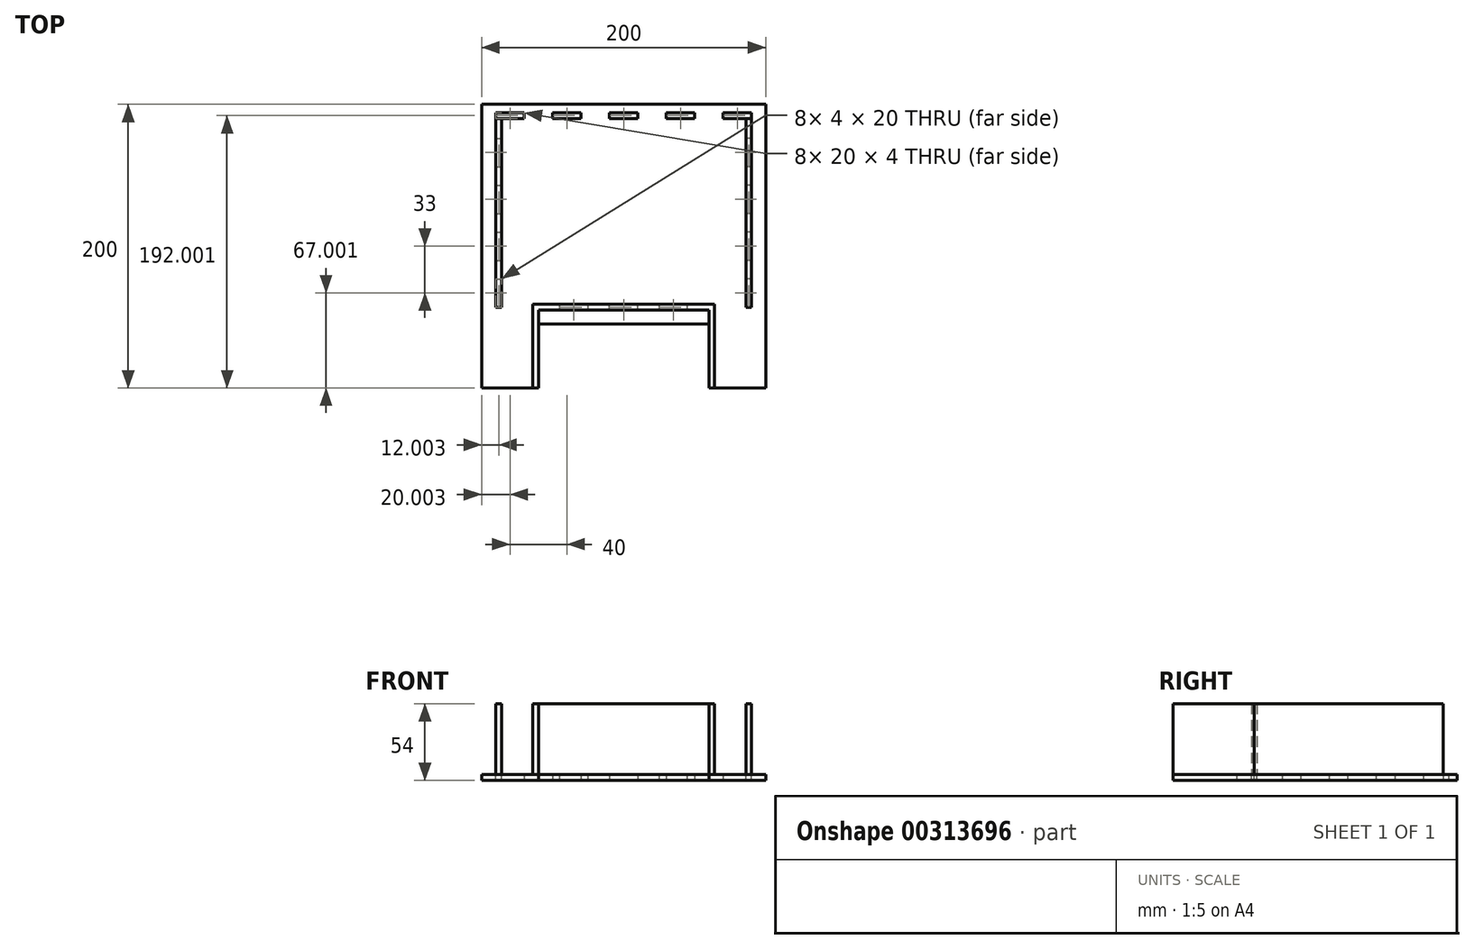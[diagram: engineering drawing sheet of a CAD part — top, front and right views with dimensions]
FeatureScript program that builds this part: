
annotation { "Feature Type Name" : "Feature", "Feature Type Description" : "" }
export const myFeature = defineFeature(function(context is Context, id is Id, definition is map)
    precondition{}
    {
        {
            var Q0;
            Q0=qCreatedBy(makeId("Top.planeOp"),FACE);
            var sketch = newSketch(context, id + "F0", { "sketchPlane" : qUnion([Q0])});
            skLineSegment(sketch, "E0.bottom", {"start": v(-97.63, 105.11) * mm, "end": v(102.37, 105.11) * mm});
            skLineSegment(sketch, "E0.top", {"start": v(-97.63, -94.89) * mm, "end": v(102.37, -94.89) * mm});
            skLineSegment(sketch, "E0.left", {"start": v(-97.63, 105.11) * mm, "end": v(-97.63, -94.89) * mm});
            skLineSegment(sketch, "E0.right", {"start": v(102.37, 105.11) * mm, "end": v(102.37, -94.89) * mm});
            skPoint(sketch, "E0.middle", {"position": v(2.37, 5.11) * mm});
            skLineSegment(sketch, "E1", {"start": v(2.37, -94.89) * mm, "end": v(2.37, 90.11) * mm, "construction": true});
            skLineSegment(sketch, "E2", {"start": v(2.37, 105.11) * mm, "end": v(2.37, 99.11) * mm, "construction": true});
            skLineSegment(sketch, "E3.direction2", {"start": v(12.37, 90.11) * mm, "end": v(13.2, -89.89) * mm, "construction": true});
            skLineSegment(sketch, "E4", {"start": v(102.37, 5.11) * mm, "end": v(92.37, 5.11) * mm, "construction": true});
            skLineSegment(sketch, "E5", {"start": v(92.37, 5.11) * mm, "end": v(102.37, 5.11) * mm, "construction": true});
            skLineSegment(sketch, "E6.top", {"start": v(92.37, -4.89) * mm, "end": v(88.37, -4.89) * mm});
            skLineSegment(sketch, "E6.left", {"start": v(92.37, 5.11) * mm, "end": v(92.37, -4.89) * mm});
            skLineSegment(sketch, "E6.right", {"start": v(88.37, 5.11) * mm, "end": v(88.37, -4.89) * mm});
            skLineSegment(sketch, "E7.MirrorCS", {"start": v(88.37, 5.11) * mm, "end": v(88.37, 15.11) * mm});
            skLineSegment(sketch, "E8.MirrorCS", {"start": v(92.37, 5.11) * mm, "end": v(92.37, 15.11) * mm});
            skLineSegment(sketch, "E9.MirrorCS", {"start": v(92.37, 15.11) * mm, "end": v(88.37, 15.11) * mm});
            skLineSegment(sketch, "E10.trimOffspring", {"start": v(88.37, 5.11) * mm, "end": v(-97.63, 5.11) * mm, "construction": true});
            skLineSegment(sketch, "E11.0.1.0", {"start": v(88.37, 38.11) * mm, "end": v(88.37, 48.11) * mm});
            skLineSegment(sketch, "E11.0.1.1", {"start": v(92.37, 48.11) * mm, "end": v(88.37, 48.11) * mm});
            skLineSegment(sketch, "E11.0.1.2", {"start": v(92.37, 38.11) * mm, "end": v(92.37, 28.11) * mm});
            skLineSegment(sketch, "E11.0.1.3", {"start": v(88.37, 38.11) * mm, "end": v(88.37, 28.11) * mm});
            skLineSegment(sketch, "E11.0.1.4", {"start": v(92.37, 28.11) * mm, "end": v(88.37, 28.11) * mm});
            skLineSegment(sketch, "E11.0.1.5", {"start": v(92.37, 38.11) * mm, "end": v(92.37, 48.11) * mm});
            skLineSegment(sketch, "E11.0.2.0", {"start": v(88.37, 71.11) * mm, "end": v(88.37, 81.11) * mm});
            skLineSegment(sketch, "E11.0.2.1", {"start": v(92.37, 81.11) * mm, "end": v(88.37, 81.11) * mm});
            skLineSegment(sketch, "E11.0.2.2", {"start": v(92.37, 71.11) * mm, "end": v(92.37, 61.11) * mm});
            skLineSegment(sketch, "E11.0.2.3", {"start": v(88.37, 71.11) * mm, "end": v(88.37, 61.11) * mm});
            skLineSegment(sketch, "E11.0.2.4", {"start": v(92.37, 61.11) * mm, "end": v(88.37, 61.11) * mm});
            skLineSegment(sketch, "E11.0.2.5", {"start": v(92.37, 71.11) * mm, "end": v(92.37, 81.11) * mm});
            skLineSegment(sketch, "E11.direction1", {"start": v(88.37, 5.11) * mm, "end": v(112.37, 5.11) * mm, "construction": true});
            skLineSegment(sketch, "E11.direction2", {"start": v(88.37, 5.11) * mm, "end": v(88.37, 38.11) * mm, "construction": true});
            skLineSegment(sketch, "E12.MirrorCS", {"start": v(92.37, -27.89) * mm, "end": v(92.37, -37.89) * mm});
            skLineSegment(sketch, "E13.MirrorCS", {"start": v(92.37, -17.89) * mm, "end": v(88.37, -17.89) * mm});
            skLineSegment(sketch, "E14.MirrorCS", {"start": v(88.37, -27.89) * mm, "end": v(88.37, -17.89) * mm});
            skLineSegment(sketch, "E15.MirrorCS", {"start": v(88.37, -27.89) * mm, "end": v(88.37, -37.89) * mm});
            skLineSegment(sketch, "E16.MirrorCS", {"start": v(92.37, -27.89) * mm, "end": v(92.37, -17.89) * mm});
            skLineSegment(sketch, "E17.MirrorCS", {"start": v(92.37, -37.89) * mm, "end": v(88.37, -37.89) * mm});
            skLineSegment(sketch, "E18.MirrorCS", {"start": v(-87.63, 15.11) * mm, "end": v(-83.63, 15.11) * mm});
            skLineSegment(sketch, "E19.MirrorCS", {"start": v(-87.63, -27.89) * mm, "end": v(-87.63, -17.89) * mm});
            skLineSegment(sketch, "E20.MirrorCS", {"start": v(-87.63, -17.89) * mm, "end": v(-83.63, -17.89) * mm});
            skLineSegment(sketch, "E21.MirrorCS", {"start": v(-87.63, 28.11) * mm, "end": v(-83.63, 28.11) * mm});
            skLineSegment(sketch, "E22.MirrorCS", {"start": v(-87.63, 81.11) * mm, "end": v(-83.63, 81.11) * mm});
            skLineSegment(sketch, "E23.MirrorCS", {"start": v(-87.63, -4.89) * mm, "end": v(-83.63, -4.89) * mm});
            skLineSegment(sketch, "E24.MirrorCS", {"start": v(-87.63, -37.89) * mm, "end": v(-83.63, -37.89) * mm});
            skLineSegment(sketch, "E25.MirrorCS", {"start": v(-83.63, 71.11) * mm, "end": v(-83.63, 61.11) * mm});
            skLineSegment(sketch, "E26.MirrorCS", {"start": v(-87.63, 61.11) * mm, "end": v(-83.63, 61.11) * mm});
            skLineSegment(sketch, "E27.MirrorCS", {"start": v(-87.63, 48.11) * mm, "end": v(-83.63, 48.11) * mm});
            skLineSegment(sketch, "E28.MirrorCS", {"start": v(-87.63, 71.11) * mm, "end": v(-87.63, 61.11) * mm});
            skLineSegment(sketch, "E29.MirrorCS", {"start": v(-83.63, -27.89) * mm, "end": v(-83.63, -17.89) * mm});
            skLineSegment(sketch, "E30.MirrorCS", {"start": v(-83.63, 5.11) * mm, "end": v(-83.63, 15.11) * mm});
            skLineSegment(sketch, "E31.MirrorCS", {"start": v(-83.63, 38.11) * mm, "end": v(-83.63, 28.11) * mm});
            skLineSegment(sketch, "E32.MirrorCS", {"start": v(-87.63, -27.89) * mm, "end": v(-87.63, -37.89) * mm});
            skLineSegment(sketch, "E33.MirrorCS", {"start": v(-87.63, 38.11) * mm, "end": v(-87.63, 48.11) * mm});
            skLineSegment(sketch, "E34.MirrorCS", {"start": v(-83.63, 71.11) * mm, "end": v(-83.63, 81.11) * mm});
            skLineSegment(sketch, "E35.MirrorCS", {"start": v(-83.63, 5.11) * mm, "end": v(-83.63, 38.11) * mm, "construction": true});
            skLineSegment(sketch, "E36.MirrorCS", {"start": v(-87.63, 5.11) * mm, "end": v(-87.63, 15.11) * mm});
            skLineSegment(sketch, "E37.MirrorCS", {"start": v(-83.63, -27.89) * mm, "end": v(-83.63, -37.89) * mm});
            skLineSegment(sketch, "E38.MirrorCS", {"start": v(-87.63, 71.11) * mm, "end": v(-87.63, 81.11) * mm});
            skLineSegment(sketch, "E39.MirrorCS", {"start": v(-83.63, 38.11) * mm, "end": v(-83.63, 48.11) * mm});
            skLineSegment(sketch, "E40.MirrorCS", {"start": v(-83.63, 5.11) * mm, "end": v(-83.63, -4.89) * mm});
            skLineSegment(sketch, "E41.MirrorCS", {"start": v(-87.63, 38.11) * mm, "end": v(-87.63, 28.11) * mm});
            skLineSegment(sketch, "E42.MirrorCS", {"start": v(-87.63, 5.11) * mm, "end": v(-87.63, -4.89) * mm});
            skLineSegment(sketch, "E43.bottom", {"start": v(2.37, 95.11) * mm, "end": v(12.37, 95.11) * mm});
            skLineSegment(sketch, "E43.top", {"start": v(2.37, 99.11) * mm, "end": v(12.37, 99.11) * mm});
            skLineSegment(sketch, "E43.right", {"start": v(12.37, 95.11) * mm, "end": v(12.37, 99.11) * mm});
            skLineSegment(sketch, "E44.MirrorCS", {"start": v(2.37, 99.11) * mm, "end": v(-7.63, 99.11) * mm});
            skLineSegment(sketch, "E45.MirrorCS", {"start": v(-7.63, 95.11) * mm, "end": v(-7.63, 99.11) * mm});
            skLineSegment(sketch, "E46.MirrorCS", {"start": v(2.37, 95.11) * mm, "end": v(-7.63, 95.11) * mm});
            skPoint(sketch, "E47.orphan", {"position": v(2.37, 95.11) * mm});
            skLineSegment(sketch, "E48.1.0.0", {"start": v(42.37, 95.11) * mm, "end": v(32.37, 95.11) * mm});
            skLineSegment(sketch, "E48.1.0.1", {"start": v(32.37, 95.11) * mm, "end": v(32.37, 99.11) * mm});
            skLineSegment(sketch, "E48.1.0.2", {"start": v(52.37, 95.11) * mm, "end": v(52.37, 99.11) * mm});
            skLineSegment(sketch, "E48.1.0.3", {"start": v(42.37, 95.11) * mm, "end": v(52.37, 95.11) * mm});
            skLineSegment(sketch, "E48.1.0.4", {"start": v(42.37, 99.11) * mm, "end": v(32.37, 99.11) * mm});
            skLineSegment(sketch, "E48.1.0.5", {"start": v(42.37, 99.11) * mm, "end": v(52.37, 99.11) * mm});
            skPoint(sketch, "E48.1.0.6", {"position": v(42.37, 95.11) * mm});
            skLineSegment(sketch, "E48.2.0.0", {"start": v(82.37, 95.11) * mm, "end": v(72.37, 95.11) * mm});
            skLineSegment(sketch, "E48.2.0.1", {"start": v(72.37, 95.11) * mm, "end": v(72.37, 99.11) * mm});
            skLineSegment(sketch, "E48.2.0.2", {"start": v(92.37, 95.11) * mm, "end": v(92.37, 99.11) * mm});
            skLineSegment(sketch, "E48.2.0.3", {"start": v(82.37, 95.11) * mm, "end": v(92.37, 95.11) * mm});
            skLineSegment(sketch, "E48.2.0.4", {"start": v(82.37, 99.11) * mm, "end": v(72.37, 99.11) * mm});
            skLineSegment(sketch, "E48.2.0.5", {"start": v(82.37, 99.11) * mm, "end": v(92.37, 99.11) * mm});
            skPoint(sketch, "E48.2.0.6", {"position": v(82.37, 95.11) * mm});
            skLineSegment(sketch, "E48.direction1", {"start": v(-7.63, 95.11) * mm, "end": v(32.37, 95.11) * mm, "construction": true});
            skPoint(sketch, "E49.MirrorP", {"position": v(-37.63, 95.11) * mm});
            skLineSegment(sketch, "E50.MirrorCS", {"start": v(-77.63, 95.11) * mm, "end": v(-87.63, 95.11) * mm});
            skLineSegment(sketch, "E51.MirrorCS", {"start": v(-37.63, 95.11) * mm, "end": v(-47.63, 95.11) * mm});
            skLineSegment(sketch, "E52.MirrorCS", {"start": v(-47.63, 95.11) * mm, "end": v(-47.63, 99.11) * mm});
            skLineSegment(sketch, "E53.MirrorCS", {"start": v(-77.63, 95.11) * mm, "end": v(-67.63, 95.11) * mm});
            skLineSegment(sketch, "E54.MirrorCS", {"start": v(-37.63, 99.11) * mm, "end": v(-47.63, 99.11) * mm});
            skLineSegment(sketch, "E55.MirrorCS", {"start": v(-37.63, 99.11) * mm, "end": v(-27.63, 99.11) * mm});
            skLineSegment(sketch, "E56.MirrorCS", {"start": v(-77.63, 99.11) * mm, "end": v(-87.63, 99.11) * mm});
            skLineSegment(sketch, "E57.MirrorCS", {"start": v(-77.63, 99.11) * mm, "end": v(-67.63, 99.11) * mm});
            skLineSegment(sketch, "E58.MirrorCS", {"start": v(-87.63, 95.11) * mm, "end": v(-87.63, 99.11) * mm});
            skPoint(sketch, "E59.MirrorP", {"position": v(-77.63, 95.11) * mm});
            skLineSegment(sketch, "E60.MirrorCS", {"start": v(-27.63, 95.11) * mm, "end": v(-27.63, 99.11) * mm});
            skLineSegment(sketch, "E61.MirrorCS", {"start": v(-67.63, 95.11) * mm, "end": v(-67.63, 99.11) * mm});
            skLineSegment(sketch, "E62.MirrorCS", {"start": v(-37.63, 95.11) * mm, "end": v(-27.63, 95.11) * mm});
            skLineSegment(sketch, "E63.MirrorCS", {"start": v(-83.63, 5.11) * mm, "end": v(102.37, 5.11) * mm, "construction": true});
            skSolve(sketch);
        }
        {
            var Q0;
            Q0=qSketchRegion(id+"F0",true);
            extrude(context, id + "F1", {"entities" : qUnion([Q0]), "endBound" : BoundingType.SYMMETRIC, "depth" : 4 * mm});
        }
        {
            var Q0;
            Q0=makeQuery(id+"F1.opExtrude","CAP_FACE",FACE,{"disambiguationData":[OSD([sQuery(id+"F0.wireOp",EDGE,"E0.bottom"),sQuery(id+"F0.wireOp",EDGE,"E0.top"),sQuery(id+"F0.wireOp",EDGE,"E0.left"),sQuery(id+"F0.wireOp",EDGE,"E0.right"),sQuery(id+"F0.wireOp",EDGE,"E6.top"),sQuery(id+"F0.wireOp",EDGE,"E6.left"),sQuery(id+"F0.wireOp",EDGE,"E6.right"),sQuery(id+"F0.wireOp",EDGE,"E7.MirrorCS"),sQuery(id+"F0.wireOp",EDGE,"E8.MirrorCS"),sQuery(id+"F0.wireOp",EDGE,"E9.MirrorCS"),sQuery(id+"F0.wireOp",EDGE,"E11.0.1.0"),sQuery(id+"F0.wireOp",EDGE,"E11.0.1.1"),sQuery(id+"F0.wireOp",EDGE,"E11.0.1.2"),sQuery(id+"F0.wireOp",EDGE,"E11.0.1.3"),sQuery(id+"F0.wireOp",EDGE,"E11.0.1.4"),sQuery(id+"F0.wireOp",EDGE,"E11.0.1.5"),sQuery(id+"F0.wireOp",EDGE,"E11.0.2.0"),sQuery(id+"F0.wireOp",EDGE,"E11.0.2.1"),sQuery(id+"F0.wireOp",EDGE,"E11.0.2.2"),sQuery(id+"F0.wireOp",EDGE,"E11.0.2.3"),sQuery(id+"F0.wireOp",EDGE,"E11.0.2.4"),sQuery(id+"F0.wireOp",EDGE,"E11.0.2.5"),sQuery(id+"F0.wireOp",EDGE,"E12.MirrorCS"),sQuery(id+"F0.wireOp",EDGE,"E13.MirrorCS"),sQuery(id+"F0.wireOp",EDGE,"a5cf8296-6a1a-48b5-a17e-63ac2f100e7a.MirrorCS"),sQuery(id+"F0.wireOp",EDGE,"6454bcc7-548b-423b-bd61-f2daa2ac8bc2.MirrorCS"),sQuery(id+"F0.wireOp",EDGE,"E14.MirrorCS"),sQuery(id+"F0.wireOp",EDGE,"9c8714bc-c0c6-4e73-bc6f-7604c54330c3.MirrorCS"),sQuery(id+"F0.wireOp",EDGE,"E15.MirrorCS"),sQuery(id+"F0.wireOp",EDGE,"E16.MirrorCS"),sQuery(id+"F0.wireOp",EDGE,"13b4a6b3-9c6c-4970-82ba-403fbf399970.MirrorCS"),sQuery(id+"F0.wireOp",EDGE,"51e258c3-53c8-4c74-be8b-1a210a0881ed.MirrorCS"),sQuery(id+"F0.wireOp",EDGE,"466627d0-206a-413f-a7e9-9d98ee74cc6c.MirrorCS"),sQuery(id+"F0.wireOp",EDGE,"E17.MirrorCS"),sQuery(id+"F0.wireOp",EDGE,"E18.MirrorCS"),sQuery(id+"F0.wireOp",EDGE,"E19.MirrorCS"),sQuery(id+"F0.wireOp",EDGE,"E20.MirrorCS"),sQuery(id+"F0.wireOp",EDGE,"f82beb81-8050-46b6-9a8f-d50cd8b2f4aa.MirrorCS"),sQuery(id+"F0.wireOp",EDGE,"E21.MirrorCS"),sQuery(id+"F0.wireOp",EDGE,"E22.MirrorCS"),sQuery(id+"F0.wireOp",EDGE,"E23.MirrorCS"),sQuery(id+"F0.wireOp",EDGE,"E24.MirrorCS"),sQuery(id+"F0.wireOp",EDGE,"350f11ef-bac5-4566-a7bd-23c74bd45e33.MirrorCS"),sQuery(id+"F0.wireOp",EDGE,"E25.MirrorCS"),sQuery(id+"F0.wireOp",EDGE,"579f2c8e-3274-4fd2-a240-7e44fb226743.MirrorCS"),sQuery(id+"F0.wireOp",EDGE,"E26.MirrorCS"),sQuery(id+"F0.wireOp",EDGE,"24017de7-ebaf-49ac-bcd0-21bb546df799.MirrorCS"),sQuery(id+"F0.wireOp",EDGE,"E27.MirrorCS"),sQuery(id+"F0.wireOp",EDGE,"E28.MirrorCS"),sQuery(id+"F0.wireOp",EDGE,"E29.MirrorCS"),sQuery(id+"F0.wireOp",EDGE,"E30.MirrorCS"),sQuery(id+"F0.wireOp",EDGE,"E31.MirrorCS"),sQuery(id+"F0.wireOp",EDGE,"E32.MirrorCS"),sQuery(id+"F0.wireOp",EDGE,"E33.MirrorCS"),sQuery(id+"F0.wireOp",EDGE,"6270afa9-d4fe-4bc2-898e-67fac00a2f92.MirrorCS"),sQuery(id+"F0.wireOp",EDGE,"E34.MirrorCS"),sQuery(id+"F0.wireOp",EDGE,"E36.MirrorCS"),sQuery(id+"F0.wireOp",EDGE,"E37.MirrorCS"),sQuery(id+"F0.wireOp",EDGE,"E38.MirrorCS"),sQuery(id+"F0.wireOp",EDGE,"E39.MirrorCS"),sQuery(id+"F0.wireOp",EDGE,"E40.MirrorCS"),sQuery(id+"F0.wireOp",EDGE,"E41.MirrorCS"),sQuery(id+"F0.wireOp",EDGE,"E42.MirrorCS"),sQuery(id+"F0.wireOp",EDGE,"c7332622-d526-407a-969b-2bd519e8cb4e.MirrorCS"),sQuery(id+"F0.wireOp",EDGE,"E43.bottom"),sQuery(id+"F0.wireOp",EDGE,"E43.top"),sQuery(id+"F0.wireOp",EDGE,"E43.right"),sQuery(id+"F0.wireOp",EDGE,"E44.MirrorCS"),sQuery(id+"F0.wireOp",EDGE,"E45.MirrorCS"),sQuery(id+"F0.wireOp",EDGE,"E46.MirrorCS"),sQuery(id+"F0.wireOp",EDGE,"E48.1.0.0"),sQuery(id+"F0.wireOp",EDGE,"E48.1.0.1"),sQuery(id+"F0.wireOp",EDGE,"E48.1.0.2"),sQuery(id+"F0.wireOp",EDGE,"E48.1.0.3"),sQuery(id+"F0.wireOp",EDGE,"E48.1.0.4"),sQuery(id+"F0.wireOp",EDGE,"E48.1.0.5"),sQuery(id+"F0.wireOp",EDGE,"E48.2.0.0"),sQuery(id+"F0.wireOp",EDGE,"E48.2.0.1"),sQuery(id+"F0.wireOp",EDGE,"E48.2.0.2"),sQuery(id+"F0.wireOp",EDGE,"E48.2.0.3"),sQuery(id+"F0.wireOp",EDGE,"E48.2.0.4"),sQuery(id+"F0.wireOp",EDGE,"E48.2.0.5"),sQuery(id+"F0.wireOp",EDGE,"E50.MirrorCS"),sQuery(id+"F0.wireOp",EDGE,"E51.MirrorCS"),sQuery(id+"F0.wireOp",EDGE,"E52.MirrorCS"),sQuery(id+"F0.wireOp",EDGE,"E53.MirrorCS"),sQuery(id+"F0.wireOp",EDGE,"E54.MirrorCS"),sQuery(id+"F0.wireOp",EDGE,"E55.MirrorCS"),sQuery(id+"F0.wireOp",EDGE,"E56.MirrorCS"),sQuery(id+"F0.wireOp",EDGE,"E57.MirrorCS"),sQuery(id+"F0.wireOp",EDGE,"E58.MirrorCS"),sQuery(id+"F0.wireOp",EDGE,"E60.MirrorCS"),sQuery(id+"F0.wireOp",EDGE,"E61.MirrorCS"),sQuery(id+"F0.wireOp",EDGE,"E62.MirrorCS")])],"isStart":false});
            var sketch = newSketch(context, id + "F2", { "sketchPlane" : qUnion([Q0])});
            skPoint(sketch, "E64", {"position": v(2.37, -94.89) * mm});
            skLineSegment(sketch, "E65", {"start": v(2.37, -94.89) * mm, "end": v(2.37, -49.89) * mm, "construction": true});
            skLineSegment(sketch, "E66", {"start": v(2.37, -49.89) * mm, "end": v(62.37, -49.89) * mm});
            skLineSegment(sketch, "E67", {"start": v(62.37, -49.89) * mm, "end": v(62.37, -94.89) * mm});
            skLineSegment(sketch, "E68", {"start": v(62.37, -94.89) * mm, "end": v(2.37, -94.89) * mm});
            skLineSegment(sketch, "E69.MirrorCS", {"start": v(2.37, -49.89) * mm, "end": v(-57.63, -49.89) * mm});
            skLineSegment(sketch, "E70.MirrorCS", {"start": v(-57.63, -49.89) * mm, "end": v(-57.63, -94.89) * mm});
            skLineSegment(sketch, "E71.MirrorCS", {"start": v(-57.63, -94.89) * mm, "end": v(2.37, -94.89) * mm});
            skSolve(sketch);
        }
        {
            var Q0;
            Q0=qSketchRegion(id+"F2",true);
            var Q1;
            Q1=makeQuery(id+"F1.opExtrude","SWEPT_BODY",BODY,{"disambiguationData":[OSD([sQuery(id+"F0.wireOp",EDGE,"E0.bottom"),sQuery(id+"F0.wireOp",EDGE,"E0.top"),sQuery(id+"F0.wireOp",EDGE,"E0.left"),sQuery(id+"F0.wireOp",EDGE,"E0.right"),sQuery(id+"F0.wireOp",EDGE,"E6.top"),sQuery(id+"F0.wireOp",EDGE,"E6.left"),sQuery(id+"F0.wireOp",EDGE,"E6.right"),sQuery(id+"F0.wireOp",EDGE,"E7.MirrorCS"),sQuery(id+"F0.wireOp",EDGE,"E8.MirrorCS"),sQuery(id+"F0.wireOp",EDGE,"E9.MirrorCS"),sQuery(id+"F0.wireOp",EDGE,"E11.0.1.0"),sQuery(id+"F0.wireOp",EDGE,"E11.0.1.1"),sQuery(id+"F0.wireOp",EDGE,"E11.0.1.2"),sQuery(id+"F0.wireOp",EDGE,"E11.0.1.3"),sQuery(id+"F0.wireOp",EDGE,"E11.0.1.4"),sQuery(id+"F0.wireOp",EDGE,"E11.0.1.5"),sQuery(id+"F0.wireOp",EDGE,"E11.0.2.0"),sQuery(id+"F0.wireOp",EDGE,"E11.0.2.1"),sQuery(id+"F0.wireOp",EDGE,"E11.0.2.2"),sQuery(id+"F0.wireOp",EDGE,"E11.0.2.3"),sQuery(id+"F0.wireOp",EDGE,"E11.0.2.4"),sQuery(id+"F0.wireOp",EDGE,"E11.0.2.5"),sQuery(id+"F0.wireOp",EDGE,"E12.MirrorCS"),sQuery(id+"F0.wireOp",EDGE,"E13.MirrorCS"),sQuery(id+"F0.wireOp",EDGE,"a5cf8296-6a1a-48b5-a17e-63ac2f100e7a.MirrorCS"),sQuery(id+"F0.wireOp",EDGE,"6454bcc7-548b-423b-bd61-f2daa2ac8bc2.MirrorCS"),sQuery(id+"F0.wireOp",EDGE,"E14.MirrorCS"),sQuery(id+"F0.wireOp",EDGE,"9c8714bc-c0c6-4e73-bc6f-7604c54330c3.MirrorCS"),sQuery(id+"F0.wireOp",EDGE,"E15.MirrorCS"),sQuery(id+"F0.wireOp",EDGE,"E16.MirrorCS"),sQuery(id+"F0.wireOp",EDGE,"13b4a6b3-9c6c-4970-82ba-403fbf399970.MirrorCS"),sQuery(id+"F0.wireOp",EDGE,"51e258c3-53c8-4c74-be8b-1a210a0881ed.MirrorCS"),sQuery(id+"F0.wireOp",EDGE,"466627d0-206a-413f-a7e9-9d98ee74cc6c.MirrorCS"),sQuery(id+"F0.wireOp",EDGE,"E17.MirrorCS"),sQuery(id+"F0.wireOp",EDGE,"E18.MirrorCS"),sQuery(id+"F0.wireOp",EDGE,"E19.MirrorCS"),sQuery(id+"F0.wireOp",EDGE,"E20.MirrorCS"),sQuery(id+"F0.wireOp",EDGE,"f82beb81-8050-46b6-9a8f-d50cd8b2f4aa.MirrorCS"),sQuery(id+"F0.wireOp",EDGE,"E21.MirrorCS"),sQuery(id+"F0.wireOp",EDGE,"E22.MirrorCS"),sQuery(id+"F0.wireOp",EDGE,"E23.MirrorCS"),sQuery(id+"F0.wireOp",EDGE,"E24.MirrorCS"),sQuery(id+"F0.wireOp",EDGE,"350f11ef-bac5-4566-a7bd-23c74bd45e33.MirrorCS"),sQuery(id+"F0.wireOp",EDGE,"E25.MirrorCS"),sQuery(id+"F0.wireOp",EDGE,"579f2c8e-3274-4fd2-a240-7e44fb226743.MirrorCS"),sQuery(id+"F0.wireOp",EDGE,"E26.MirrorCS"),sQuery(id+"F0.wireOp",EDGE,"24017de7-ebaf-49ac-bcd0-21bb546df799.MirrorCS"),sQuery(id+"F0.wireOp",EDGE,"E27.MirrorCS"),sQuery(id+"F0.wireOp",EDGE,"E28.MirrorCS"),sQuery(id+"F0.wireOp",EDGE,"E29.MirrorCS"),sQuery(id+"F0.wireOp",EDGE,"E30.MirrorCS"),sQuery(id+"F0.wireOp",EDGE,"E31.MirrorCS"),sQuery(id+"F0.wireOp",EDGE,"E32.MirrorCS"),sQuery(id+"F0.wireOp",EDGE,"E33.MirrorCS"),sQuery(id+"F0.wireOp",EDGE,"6270afa9-d4fe-4bc2-898e-67fac00a2f92.MirrorCS"),sQuery(id+"F0.wireOp",EDGE,"E34.MirrorCS"),sQuery(id+"F0.wireOp",EDGE,"E36.MirrorCS"),sQuery(id+"F0.wireOp",EDGE,"E37.MirrorCS"),sQuery(id+"F0.wireOp",EDGE,"E38.MirrorCS"),sQuery(id+"F0.wireOp",EDGE,"E39.MirrorCS"),sQuery(id+"F0.wireOp",EDGE,"E40.MirrorCS"),sQuery(id+"F0.wireOp",EDGE,"E41.MirrorCS"),sQuery(id+"F0.wireOp",EDGE,"E42.MirrorCS"),sQuery(id+"F0.wireOp",EDGE,"c7332622-d526-407a-969b-2bd519e8cb4e.MirrorCS"),sQuery(id+"F0.wireOp",EDGE,"E43.bottom"),sQuery(id+"F0.wireOp",EDGE,"E43.top"),sQuery(id+"F0.wireOp",EDGE,"E43.right"),sQuery(id+"F0.wireOp",EDGE,"E44.MirrorCS"),sQuery(id+"F0.wireOp",EDGE,"E45.MirrorCS"),sQuery(id+"F0.wireOp",EDGE,"E46.MirrorCS"),sQuery(id+"F0.wireOp",EDGE,"E48.1.0.0"),sQuery(id+"F0.wireOp",EDGE,"E48.1.0.1"),sQuery(id+"F0.wireOp",EDGE,"E48.1.0.2"),sQuery(id+"F0.wireOp",EDGE,"E48.1.0.3"),sQuery(id+"F0.wireOp",EDGE,"E48.1.0.4"),sQuery(id+"F0.wireOp",EDGE,"E48.1.0.5"),sQuery(id+"F0.wireOp",EDGE,"E48.2.0.0"),sQuery(id+"F0.wireOp",EDGE,"E48.2.0.1"),sQuery(id+"F0.wireOp",EDGE,"E48.2.0.2"),sQuery(id+"F0.wireOp",EDGE,"E48.2.0.3"),sQuery(id+"F0.wireOp",EDGE,"E48.2.0.4"),sQuery(id+"F0.wireOp",EDGE,"E48.2.0.5"),sQuery(id+"F0.wireOp",EDGE,"E50.MirrorCS"),sQuery(id+"F0.wireOp",EDGE,"E51.MirrorCS"),sQuery(id+"F0.wireOp",EDGE,"E52.MirrorCS"),sQuery(id+"F0.wireOp",EDGE,"E53.MirrorCS"),sQuery(id+"F0.wireOp",EDGE,"E54.MirrorCS"),sQuery(id+"F0.wireOp",EDGE,"E55.MirrorCS"),sQuery(id+"F0.wireOp",EDGE,"E56.MirrorCS"),sQuery(id+"F0.wireOp",EDGE,"E57.MirrorCS"),sQuery(id+"F0.wireOp",EDGE,"E58.MirrorCS"),sQuery(id+"F0.wireOp",EDGE,"E60.MirrorCS"),sQuery(id+"F0.wireOp",EDGE,"E61.MirrorCS"),sQuery(id+"F0.wireOp",EDGE,"E62.MirrorCS")])]});
            extrude(context, id + "F3", {"entities" : qUnion([Q0]), "operationType" : NewBodyOperationType.REMOVE, "endBound" : BoundingType.UP_TO_BODY, "oppositeDirection" : true, "endBoundEntityBody" : qUnion([Q1]), "depth" : 25 * mm});
        }
        {
            var Q0;
            Q0=makeQuery(id+"F1.opExtrude","CAP_FACE",FACE,{"disambiguationData":[OSD([sQuery(id+"F0.wireOp",EDGE,"E0.bottom"),sQuery(id+"F0.wireOp",EDGE,"E0.top"),sQuery(id+"F0.wireOp",EDGE,"E0.left"),sQuery(id+"F0.wireOp",EDGE,"E0.right"),sQuery(id+"F0.wireOp",EDGE,"E6.top"),sQuery(id+"F0.wireOp",EDGE,"E6.left"),sQuery(id+"F0.wireOp",EDGE,"E6.right"),sQuery(id+"F0.wireOp",EDGE,"E7.MirrorCS"),sQuery(id+"F0.wireOp",EDGE,"E8.MirrorCS"),sQuery(id+"F0.wireOp",EDGE,"E9.MirrorCS"),sQuery(id+"F0.wireOp",EDGE,"E11.0.1.0"),sQuery(id+"F0.wireOp",EDGE,"E11.0.1.1"),sQuery(id+"F0.wireOp",EDGE,"E11.0.1.2"),sQuery(id+"F0.wireOp",EDGE,"E11.0.1.3"),sQuery(id+"F0.wireOp",EDGE,"E11.0.1.4"),sQuery(id+"F0.wireOp",EDGE,"E11.0.1.5"),sQuery(id+"F0.wireOp",EDGE,"E11.0.2.0"),sQuery(id+"F0.wireOp",EDGE,"E11.0.2.1"),sQuery(id+"F0.wireOp",EDGE,"E11.0.2.2"),sQuery(id+"F0.wireOp",EDGE,"E11.0.2.3"),sQuery(id+"F0.wireOp",EDGE,"E11.0.2.4"),sQuery(id+"F0.wireOp",EDGE,"E11.0.2.5"),sQuery(id+"F0.wireOp",EDGE,"E12.MirrorCS"),sQuery(id+"F0.wireOp",EDGE,"E13.MirrorCS"),sQuery(id+"F0.wireOp",EDGE,"E14.MirrorCS"),sQuery(id+"F0.wireOp",EDGE,"E15.MirrorCS"),sQuery(id+"F0.wireOp",EDGE,"E16.MirrorCS"),sQuery(id+"F0.wireOp",EDGE,"E17.MirrorCS"),sQuery(id+"F0.wireOp",EDGE,"E18.MirrorCS"),sQuery(id+"F0.wireOp",EDGE,"E19.MirrorCS"),sQuery(id+"F0.wireOp",EDGE,"E20.MirrorCS"),sQuery(id+"F0.wireOp",EDGE,"E21.MirrorCS"),sQuery(id+"F0.wireOp",EDGE,"E22.MirrorCS"),sQuery(id+"F0.wireOp",EDGE,"E23.MirrorCS"),sQuery(id+"F0.wireOp",EDGE,"E24.MirrorCS"),sQuery(id+"F0.wireOp",EDGE,"E25.MirrorCS"),sQuery(id+"F0.wireOp",EDGE,"E26.MirrorCS"),sQuery(id+"F0.wireOp",EDGE,"E27.MirrorCS"),sQuery(id+"F0.wireOp",EDGE,"E28.MirrorCS"),sQuery(id+"F0.wireOp",EDGE,"E29.MirrorCS"),sQuery(id+"F0.wireOp",EDGE,"E30.MirrorCS"),sQuery(id+"F0.wireOp",EDGE,"E31.MirrorCS"),sQuery(id+"F0.wireOp",EDGE,"E32.MirrorCS"),sQuery(id+"F0.wireOp",EDGE,"E33.MirrorCS"),sQuery(id+"F0.wireOp",EDGE,"E34.MirrorCS"),sQuery(id+"F0.wireOp",EDGE,"E36.MirrorCS"),sQuery(id+"F0.wireOp",EDGE,"E37.MirrorCS"),sQuery(id+"F0.wireOp",EDGE,"E38.MirrorCS"),sQuery(id+"F0.wireOp",EDGE,"E39.MirrorCS"),sQuery(id+"F0.wireOp",EDGE,"E40.MirrorCS"),sQuery(id+"F0.wireOp",EDGE,"E41.MirrorCS"),sQuery(id+"F0.wireOp",EDGE,"E42.MirrorCS"),sQuery(id+"F0.wireOp",EDGE,"E43.bottom"),sQuery(id+"F0.wireOp",EDGE,"E43.top"),sQuery(id+"F0.wireOp",EDGE,"E43.right"),sQuery(id+"F0.wireOp",EDGE,"E44.MirrorCS"),sQuery(id+"F0.wireOp",EDGE,"E45.MirrorCS"),sQuery(id+"F0.wireOp",EDGE,"E46.MirrorCS"),sQuery(id+"F0.wireOp",EDGE,"E48.1.0.0"),sQuery(id+"F0.wireOp",EDGE,"E48.1.0.1"),sQuery(id+"F0.wireOp",EDGE,"E48.1.0.2"),sQuery(id+"F0.wireOp",EDGE,"E48.1.0.3"),sQuery(id+"F0.wireOp",EDGE,"E48.1.0.4"),sQuery(id+"F0.wireOp",EDGE,"E48.1.0.5"),sQuery(id+"F0.wireOp",EDGE,"E48.2.0.0"),sQuery(id+"F0.wireOp",EDGE,"E48.2.0.1"),sQuery(id+"F0.wireOp",EDGE,"E48.2.0.2"),sQuery(id+"F0.wireOp",EDGE,"E48.2.0.3"),sQuery(id+"F0.wireOp",EDGE,"E48.2.0.4"),sQuery(id+"F0.wireOp",EDGE,"E48.2.0.5"),sQuery(id+"F0.wireOp",EDGE,"E50.MirrorCS"),sQuery(id+"F0.wireOp",EDGE,"E51.MirrorCS"),sQuery(id+"F0.wireOp",EDGE,"E52.MirrorCS"),sQuery(id+"F0.wireOp",EDGE,"E53.MirrorCS"),sQuery(id+"F0.wireOp",EDGE,"E54.MirrorCS"),sQuery(id+"F0.wireOp",EDGE,"E55.MirrorCS"),sQuery(id+"F0.wireOp",EDGE,"E56.MirrorCS"),sQuery(id+"F0.wireOp",EDGE,"E57.MirrorCS"),sQuery(id+"F0.wireOp",EDGE,"E58.MirrorCS"),sQuery(id+"F0.wireOp",EDGE,"E60.MirrorCS"),sQuery(id+"F0.wireOp",EDGE,"E61.MirrorCS"),sQuery(id+"F0.wireOp",EDGE,"E62.MirrorCS")])],"isStart":false});
            var sketch = newSketch(context, id + "F4", { "sketchPlane" : qUnion([Q0])});
            skLineSegment(sketch, "E72", {"start": v(2.37, 95.11) * mm, "end": v(2.37, -49.89) * mm, "construction": true});
            skPoint(sketch, "E73", {"position": v(2.37, -39.89) * mm});
            skLineSegment(sketch, "E74.bottom", {"start": v(2.37, -39.89) * mm, "end": v(-7.63, -39.89) * mm});
            skLineSegment(sketch, "E74.top", {"start": v(2.37, -35.89) * mm, "end": v(-7.63, -35.89) * mm});
            skLineSegment(sketch, "E74.left", {"start": v(2.37, -39.89) * mm, "end": v(2.37, -35.89) * mm});
            skLineSegment(sketch, "E74.right", {"start": v(-7.63, -39.89) * mm, "end": v(-7.63, -35.89) * mm});
            skLineSegment(sketch, "E75.MirrorCS", {"start": v(2.37, -35.89) * mm, "end": v(12.37, -35.89) * mm});
            skLineSegment(sketch, "E76.MirrorCS", {"start": v(2.37, -39.89) * mm, "end": v(12.37, -39.89) * mm});
            skLineSegment(sketch, "E77.MirrorCS", {"start": v(12.37, -39.89) * mm, "end": v(12.37, -35.89) * mm});
            skLineSegment(sketch, "E78.1.0.0", {"start": v(37.37, -35.89) * mm, "end": v(47.37, -35.89) * mm});
            skLineSegment(sketch, "E78.1.0.1", {"start": v(47.37, -39.89) * mm, "end": v(47.37, -35.89) * mm});
            skLineSegment(sketch, "E78.1.0.2", {"start": v(37.37, -39.89) * mm, "end": v(47.37, -39.89) * mm});
            skLineSegment(sketch, "E78.1.0.3", {"start": v(37.37, -39.89) * mm, "end": v(27.37, -39.89) * mm});
            skLineSegment(sketch, "E78.1.0.4", {"start": v(27.37, -39.89) * mm, "end": v(27.37, -35.89) * mm});
            skLineSegment(sketch, "E78.1.0.5", {"start": v(37.37, -35.89) * mm, "end": v(27.37, -35.89) * mm});
            skLineSegment(sketch, "E78.direction1", {"start": v(2.37, -35.89) * mm, "end": v(37.37, -35.89) * mm, "construction": true});
            skLineSegment(sketch, "E79.MirrorCS", {"start": v(-32.63, -39.89) * mm, "end": v(-22.63, -39.89) * mm});
            skLineSegment(sketch, "E80.MirrorCS", {"start": v(-32.63, -39.89) * mm, "end": v(-42.63, -39.89) * mm});
            skLineSegment(sketch, "E81.MirrorCS", {"start": v(-42.63, -39.89) * mm, "end": v(-42.63, -35.89) * mm});
            skLineSegment(sketch, "E82.MirrorCS", {"start": v(-32.63, -35.89) * mm, "end": v(-42.63, -35.89) * mm});
            skLineSegment(sketch, "E83.MirrorCS", {"start": v(-22.63, -39.89) * mm, "end": v(-22.63, -35.89) * mm});
            skLineSegment(sketch, "E84.MirrorCS", {"start": v(2.37, -35.89) * mm, "end": v(-32.63, -35.89) * mm, "construction": true});
            skLineSegment(sketch, "E85", {"start": v(-22.63, -35.89) * mm, "end": v(-32.63, -35.89) * mm});
            skSolve(sketch);
        }
        {
            var Q0;
            Q0=qSketchRegion(id+"F4",true);
            extrude(context, id + "F5", {"entities" : qUnion([Q0]), "operationType" : NewBodyOperationType.REMOVE, "oppositeDirection" : true, "depth" : 25 * mm});
        }
        {
            var Q0;
            Q0=makeQuery(id+"F1.opExtrude","CAP_FACE",FACE,{"disambiguationData":[OSD([sQuery(id+"F0.wireOp",EDGE,"E0.bottom"),sQuery(id+"F0.wireOp",EDGE,"E0.top"),sQuery(id+"F0.wireOp",EDGE,"E0.left"),sQuery(id+"F0.wireOp",EDGE,"E0.right"),sQuery(id+"F0.wireOp",EDGE,"E6.top"),sQuery(id+"F0.wireOp",EDGE,"E6.left"),sQuery(id+"F0.wireOp",EDGE,"E6.right"),sQuery(id+"F0.wireOp",EDGE,"E7.MirrorCS"),sQuery(id+"F0.wireOp",EDGE,"E8.MirrorCS"),sQuery(id+"F0.wireOp",EDGE,"E9.MirrorCS"),sQuery(id+"F0.wireOp",EDGE,"E11.0.1.0"),sQuery(id+"F0.wireOp",EDGE,"E11.0.1.1"),sQuery(id+"F0.wireOp",EDGE,"E11.0.1.2"),sQuery(id+"F0.wireOp",EDGE,"E11.0.1.3"),sQuery(id+"F0.wireOp",EDGE,"E11.0.1.4"),sQuery(id+"F0.wireOp",EDGE,"E11.0.1.5"),sQuery(id+"F0.wireOp",EDGE,"E11.0.2.0"),sQuery(id+"F0.wireOp",EDGE,"E11.0.2.1"),sQuery(id+"F0.wireOp",EDGE,"E11.0.2.2"),sQuery(id+"F0.wireOp",EDGE,"E11.0.2.3"),sQuery(id+"F0.wireOp",EDGE,"E11.0.2.4"),sQuery(id+"F0.wireOp",EDGE,"E11.0.2.5"),sQuery(id+"F0.wireOp",EDGE,"E12.MirrorCS"),sQuery(id+"F0.wireOp",EDGE,"E13.MirrorCS"),sQuery(id+"F0.wireOp",EDGE,"E14.MirrorCS"),sQuery(id+"F0.wireOp",EDGE,"E15.MirrorCS"),sQuery(id+"F0.wireOp",EDGE,"E16.MirrorCS"),sQuery(id+"F0.wireOp",EDGE,"E17.MirrorCS"),sQuery(id+"F0.wireOp",EDGE,"E18.MirrorCS"),sQuery(id+"F0.wireOp",EDGE,"E19.MirrorCS"),sQuery(id+"F0.wireOp",EDGE,"E20.MirrorCS"),sQuery(id+"F0.wireOp",EDGE,"E21.MirrorCS"),sQuery(id+"F0.wireOp",EDGE,"E22.MirrorCS"),sQuery(id+"F0.wireOp",EDGE,"E23.MirrorCS"),sQuery(id+"F0.wireOp",EDGE,"E24.MirrorCS"),sQuery(id+"F0.wireOp",EDGE,"E25.MirrorCS"),sQuery(id+"F0.wireOp",EDGE,"E26.MirrorCS"),sQuery(id+"F0.wireOp",EDGE,"E27.MirrorCS"),sQuery(id+"F0.wireOp",EDGE,"E28.MirrorCS"),sQuery(id+"F0.wireOp",EDGE,"E29.MirrorCS"),sQuery(id+"F0.wireOp",EDGE,"E30.MirrorCS"),sQuery(id+"F0.wireOp",EDGE,"E31.MirrorCS"),sQuery(id+"F0.wireOp",EDGE,"E32.MirrorCS"),sQuery(id+"F0.wireOp",EDGE,"E33.MirrorCS"),sQuery(id+"F0.wireOp",EDGE,"E34.MirrorCS"),sQuery(id+"F0.wireOp",EDGE,"E36.MirrorCS"),sQuery(id+"F0.wireOp",EDGE,"E37.MirrorCS"),sQuery(id+"F0.wireOp",EDGE,"E38.MirrorCS"),sQuery(id+"F0.wireOp",EDGE,"E39.MirrorCS"),sQuery(id+"F0.wireOp",EDGE,"E40.MirrorCS"),sQuery(id+"F0.wireOp",EDGE,"E41.MirrorCS"),sQuery(id+"F0.wireOp",EDGE,"E42.MirrorCS"),sQuery(id+"F0.wireOp",EDGE,"E43.bottom"),sQuery(id+"F0.wireOp",EDGE,"E43.top"),sQuery(id+"F0.wireOp",EDGE,"E43.right"),sQuery(id+"F0.wireOp",EDGE,"E44.MirrorCS"),sQuery(id+"F0.wireOp",EDGE,"E45.MirrorCS"),sQuery(id+"F0.wireOp",EDGE,"E46.MirrorCS"),sQuery(id+"F0.wireOp",EDGE,"E48.1.0.0"),sQuery(id+"F0.wireOp",EDGE,"E48.1.0.1"),sQuery(id+"F0.wireOp",EDGE,"E48.1.0.2"),sQuery(id+"F0.wireOp",EDGE,"E48.1.0.3"),sQuery(id+"F0.wireOp",EDGE,"E48.1.0.4"),sQuery(id+"F0.wireOp",EDGE,"E48.1.0.5"),sQuery(id+"F0.wireOp",EDGE,"E48.2.0.0"),sQuery(id+"F0.wireOp",EDGE,"E48.2.0.1"),sQuery(id+"F0.wireOp",EDGE,"E48.2.0.2"),sQuery(id+"F0.wireOp",EDGE,"E48.2.0.3"),sQuery(id+"F0.wireOp",EDGE,"E48.2.0.4"),sQuery(id+"F0.wireOp",EDGE,"E48.2.0.5"),sQuery(id+"F0.wireOp",EDGE,"E50.MirrorCS"),sQuery(id+"F0.wireOp",EDGE,"E51.MirrorCS"),sQuery(id+"F0.wireOp",EDGE,"E52.MirrorCS"),sQuery(id+"F0.wireOp",EDGE,"E53.MirrorCS"),sQuery(id+"F0.wireOp",EDGE,"E54.MirrorCS"),sQuery(id+"F0.wireOp",EDGE,"E55.MirrorCS"),sQuery(id+"F0.wireOp",EDGE,"E56.MirrorCS"),sQuery(id+"F0.wireOp",EDGE,"E57.MirrorCS"),sQuery(id+"F0.wireOp",EDGE,"E58.MirrorCS"),sQuery(id+"F0.wireOp",EDGE,"E60.MirrorCS"),sQuery(id+"F0.wireOp",EDGE,"E61.MirrorCS"),sQuery(id+"F0.wireOp",EDGE,"E62.MirrorCS")])],"isStart":false});
            var sketch = newSketch(context, id + "F6", { "sketchPlane" : qUnion([Q0])});
            skLineSegment(sketch, "E86.bottom", {"start": v(-83.63, 81.11) * mm, "end": v(-87.63, 81.11) * mm});
            skLineSegment(sketch, "E86.top", {"start": v(-83.63, 61.11) * mm, "end": v(-87.63, 61.11) * mm});
            skLineSegment(sketch, "E86.left", {"start": v(-83.63, 81.11) * mm, "end": v(-83.63, 61.11) * mm});
            skLineSegment(sketch, "E86.right", {"start": v(-87.63, 81.11) * mm, "end": v(-87.63, 61.11) * mm});
            skLineSegment(sketch, "E87.bottom", {"start": v(-83.63, 48.11) * mm, "end": v(-87.63, 48.11) * mm});
            skLineSegment(sketch, "E87.top", {"start": v(-83.63, 28.11) * mm, "end": v(-87.63, 28.11) * mm});
            skLineSegment(sketch, "E87.left", {"start": v(-83.63, 48.11) * mm, "end": v(-83.63, 28.11) * mm});
            skLineSegment(sketch, "E87.right", {"start": v(-87.63, 48.11) * mm, "end": v(-87.63, 28.11) * mm});
            skLineSegment(sketch, "E88.bottom", {"start": v(-83.63, 15.11) * mm, "end": v(-87.63, 15.11) * mm});
            skLineSegment(sketch, "E88.top", {"start": v(-83.63, -4.89) * mm, "end": v(-87.63, -4.89) * mm});
            skLineSegment(sketch, "E88.left", {"start": v(-83.63, 15.11) * mm, "end": v(-83.63, -4.89) * mm});
            skLineSegment(sketch, "E88.right", {"start": v(-87.63, 15.11) * mm, "end": v(-87.63, -4.89) * mm});
            skLineSegment(sketch, "E89.bottom", {"start": v(-83.63, -17.89) * mm, "end": v(-87.63, -17.89) * mm});
            skLineSegment(sketch, "E89.top", {"start": v(-83.63, -37.89) * mm, "end": v(-87.63, -37.89) * mm});
            skLineSegment(sketch, "E89.left", {"start": v(-83.63, -17.89) * mm, "end": v(-83.63, -37.89) * mm});
            skLineSegment(sketch, "E89.right", {"start": v(-87.63, -17.89) * mm, "end": v(-87.63, -37.89) * mm});
            skLineSegment(sketch, "E90.bottom", {"start": v(-42.63, -39.89) * mm, "end": v(-22.63, -39.89) * mm});
            skLineSegment(sketch, "E90.top", {"start": v(-42.63, -35.89) * mm, "end": v(-22.63, -35.89) * mm});
            skLineSegment(sketch, "E90.left", {"start": v(-42.63, -39.89) * mm, "end": v(-42.63, -35.89) * mm});
            skLineSegment(sketch, "E90.right", {"start": v(-22.63, -39.89) * mm, "end": v(-22.63, -35.89) * mm});
            skLineSegment(sketch, "E91.bottom", {"start": v(-7.63, -39.89) * mm, "end": v(12.37, -39.89) * mm});
            skLineSegment(sketch, "E91.top", {"start": v(-7.63, -35.89) * mm, "end": v(12.37, -35.89) * mm});
            skLineSegment(sketch, "E91.left", {"start": v(-7.63, -39.89) * mm, "end": v(-7.63, -35.89) * mm});
            skLineSegment(sketch, "E91.right", {"start": v(12.37, -39.89) * mm, "end": v(12.37, -35.89) * mm});
            skLineSegment(sketch, "E92.bottom", {"start": v(27.37, -39.89) * mm, "end": v(47.37, -39.89) * mm});
            skLineSegment(sketch, "E92.top", {"start": v(27.37, -35.89) * mm, "end": v(47.37, -35.89) * mm});
            skLineSegment(sketch, "E92.left", {"start": v(27.37, -39.89) * mm, "end": v(27.37, -35.89) * mm});
            skLineSegment(sketch, "E92.right", {"start": v(47.37, -39.89) * mm, "end": v(47.37, -35.89) * mm});
            skLineSegment(sketch, "E93.bottom", {"start": v(92.37, -37.89) * mm, "end": v(88.37, -37.89) * mm});
            skLineSegment(sketch, "E93.top", {"start": v(92.37, -17.89) * mm, "end": v(88.37, -17.89) * mm});
            skLineSegment(sketch, "E93.left", {"start": v(92.37, -37.89) * mm, "end": v(92.37, -17.89) * mm});
            skLineSegment(sketch, "E93.right", {"start": v(88.37, -37.89) * mm, "end": v(88.37, -17.89) * mm});
            skLineSegment(sketch, "E94.bottom", {"start": v(92.37, -4.89) * mm, "end": v(88.37, -4.89) * mm});
            skLineSegment(sketch, "E94.top", {"start": v(92.37, 15.11) * mm, "end": v(88.37, 15.11) * mm});
            skLineSegment(sketch, "E94.left", {"start": v(92.37, -4.89) * mm, "end": v(92.37, 15.11) * mm});
            skLineSegment(sketch, "E94.right", {"start": v(88.37, -4.89) * mm, "end": v(88.37, 15.11) * mm});
            skLineSegment(sketch, "E95.bottom", {"start": v(92.37, 28.11) * mm, "end": v(88.37, 28.11) * mm});
            skLineSegment(sketch, "E95.top", {"start": v(92.37, 48.11) * mm, "end": v(88.37, 48.11) * mm});
            skLineSegment(sketch, "E95.left", {"start": v(92.37, 28.11) * mm, "end": v(92.37, 48.11) * mm});
            skLineSegment(sketch, "E95.right", {"start": v(88.37, 28.11) * mm, "end": v(88.37, 48.11) * mm});
            skLineSegment(sketch, "E96.bottom", {"start": v(92.37, 61.11) * mm, "end": v(88.37, 61.11) * mm});
            skLineSegment(sketch, "E96.top", {"start": v(92.37, 81.11) * mm, "end": v(88.37, 81.11) * mm});
            skLineSegment(sketch, "E96.left", {"start": v(92.37, 61.11) * mm, "end": v(92.37, 81.11) * mm});
            skLineSegment(sketch, "E96.right", {"start": v(88.37, 61.11) * mm, "end": v(88.37, 81.11) * mm});
            skLineSegment(sketch, "E97.bottom", {"start": v(92.37, 99.11) * mm, "end": v(72.37, 99.11) * mm});
            skLineSegment(sketch, "E97.top", {"start": v(92.37, 95.11) * mm, "end": v(72.37, 95.11) * mm});
            skLineSegment(sketch, "E97.left", {"start": v(92.37, 99.11) * mm, "end": v(92.37, 95.11) * mm});
            skLineSegment(sketch, "E97.right", {"start": v(72.37, 99.11) * mm, "end": v(72.37, 95.11) * mm});
            skLineSegment(sketch, "E98.bottom", {"start": v(52.37, 99.11) * mm, "end": v(32.37, 99.11) * mm});
            skLineSegment(sketch, "E98.top", {"start": v(52.37, 95.11) * mm, "end": v(32.37, 95.11) * mm});
            skLineSegment(sketch, "E98.left", {"start": v(52.37, 99.11) * mm, "end": v(52.37, 95.11) * mm});
            skLineSegment(sketch, "E98.right", {"start": v(32.37, 99.11) * mm, "end": v(32.37, 95.11) * mm});
            skLineSegment(sketch, "E99.bottom", {"start": v(12.37, 99.11) * mm, "end": v(-7.63, 99.11) * mm});
            skLineSegment(sketch, "E99.top", {"start": v(12.37, 95.11) * mm, "end": v(-7.63, 95.11) * mm});
            skLineSegment(sketch, "E99.left", {"start": v(12.37, 99.11) * mm, "end": v(12.37, 95.11) * mm});
            skLineSegment(sketch, "E99.right", {"start": v(-7.63, 99.11) * mm, "end": v(-7.63, 95.11) * mm});
            skLineSegment(sketch, "E100.bottom", {"start": v(-27.63, 99.11) * mm, "end": v(-47.63, 99.11) * mm});
            skLineSegment(sketch, "E100.top", {"start": v(-27.63, 95.11) * mm, "end": v(-47.63, 95.11) * mm});
            skLineSegment(sketch, "E100.left", {"start": v(-27.63, 99.11) * mm, "end": v(-27.63, 95.11) * mm});
            skLineSegment(sketch, "E100.right", {"start": v(-47.63, 99.11) * mm, "end": v(-47.63, 95.11) * mm});
            skLineSegment(sketch, "E101.bottom", {"start": v(-67.63, 99.11) * mm, "end": v(-87.63, 99.11) * mm});
            skLineSegment(sketch, "E101.top", {"start": v(-67.63, 95.11) * mm, "end": v(-87.63, 95.11) * mm});
            skLineSegment(sketch, "E101.left", {"start": v(-67.63, 99.11) * mm, "end": v(-67.63, 95.11) * mm});
            skLineSegment(sketch, "E101.right", {"start": v(-87.63, 99.11) * mm, "end": v(-87.63, 95.11) * mm});
            skSolve(sketch);
        }
        {
            var Q0;
            Q0=qSketchRegion(id+"F6",true);
            extrude(context, id + "F7", {"entities" : qUnion([Q0]), "oppositeDirection" : true, "depth" : 4 * mm});
        }
        {
            var Q0;
            Q0=makeQuery(id+"F1.opExtrude","CAP_FACE",FACE,{"disambiguationData":[OSD([sQuery(id+"F0.wireOp",EDGE,"E0.bottom"),sQuery(id+"F0.wireOp",EDGE,"E0.top"),sQuery(id+"F0.wireOp",EDGE,"E0.left"),sQuery(id+"F0.wireOp",EDGE,"E0.right"),sQuery(id+"F0.wireOp",EDGE,"E6.top"),sQuery(id+"F0.wireOp",EDGE,"E6.left"),sQuery(id+"F0.wireOp",EDGE,"E6.right"),sQuery(id+"F0.wireOp",EDGE,"E7.MirrorCS"),sQuery(id+"F0.wireOp",EDGE,"E8.MirrorCS"),sQuery(id+"F0.wireOp",EDGE,"E9.MirrorCS"),sQuery(id+"F0.wireOp",EDGE,"E11.0.1.0"),sQuery(id+"F0.wireOp",EDGE,"E11.0.1.1"),sQuery(id+"F0.wireOp",EDGE,"E11.0.1.2"),sQuery(id+"F0.wireOp",EDGE,"E11.0.1.3"),sQuery(id+"F0.wireOp",EDGE,"E11.0.1.4"),sQuery(id+"F0.wireOp",EDGE,"E11.0.1.5"),sQuery(id+"F0.wireOp",EDGE,"E11.0.2.0"),sQuery(id+"F0.wireOp",EDGE,"E11.0.2.1"),sQuery(id+"F0.wireOp",EDGE,"E11.0.2.2"),sQuery(id+"F0.wireOp",EDGE,"E11.0.2.3"),sQuery(id+"F0.wireOp",EDGE,"E11.0.2.4"),sQuery(id+"F0.wireOp",EDGE,"E11.0.2.5"),sQuery(id+"F0.wireOp",EDGE,"E12.MirrorCS"),sQuery(id+"F0.wireOp",EDGE,"E13.MirrorCS"),sQuery(id+"F0.wireOp",EDGE,"E14.MirrorCS"),sQuery(id+"F0.wireOp",EDGE,"E15.MirrorCS"),sQuery(id+"F0.wireOp",EDGE,"E16.MirrorCS"),sQuery(id+"F0.wireOp",EDGE,"E17.MirrorCS"),sQuery(id+"F0.wireOp",EDGE,"E18.MirrorCS"),sQuery(id+"F0.wireOp",EDGE,"E19.MirrorCS"),sQuery(id+"F0.wireOp",EDGE,"E20.MirrorCS"),sQuery(id+"F0.wireOp",EDGE,"E21.MirrorCS"),sQuery(id+"F0.wireOp",EDGE,"E22.MirrorCS"),sQuery(id+"F0.wireOp",EDGE,"E23.MirrorCS"),sQuery(id+"F0.wireOp",EDGE,"E24.MirrorCS"),sQuery(id+"F0.wireOp",EDGE,"E25.MirrorCS"),sQuery(id+"F0.wireOp",EDGE,"E26.MirrorCS"),sQuery(id+"F0.wireOp",EDGE,"E27.MirrorCS"),sQuery(id+"F0.wireOp",EDGE,"E28.MirrorCS"),sQuery(id+"F0.wireOp",EDGE,"E29.MirrorCS"),sQuery(id+"F0.wireOp",EDGE,"E30.MirrorCS"),sQuery(id+"F0.wireOp",EDGE,"E31.MirrorCS"),sQuery(id+"F0.wireOp",EDGE,"E32.MirrorCS"),sQuery(id+"F0.wireOp",EDGE,"E33.MirrorCS"),sQuery(id+"F0.wireOp",EDGE,"E34.MirrorCS"),sQuery(id+"F0.wireOp",EDGE,"E36.MirrorCS"),sQuery(id+"F0.wireOp",EDGE,"E37.MirrorCS"),sQuery(id+"F0.wireOp",EDGE,"E38.MirrorCS"),sQuery(id+"F0.wireOp",EDGE,"E39.MirrorCS"),sQuery(id+"F0.wireOp",EDGE,"E40.MirrorCS"),sQuery(id+"F0.wireOp",EDGE,"E41.MirrorCS"),sQuery(id+"F0.wireOp",EDGE,"E42.MirrorCS"),sQuery(id+"F0.wireOp",EDGE,"E43.bottom"),sQuery(id+"F0.wireOp",EDGE,"E43.top"),sQuery(id+"F0.wireOp",EDGE,"E43.right"),sQuery(id+"F0.wireOp",EDGE,"E44.MirrorCS"),sQuery(id+"F0.wireOp",EDGE,"E45.MirrorCS"),sQuery(id+"F0.wireOp",EDGE,"E46.MirrorCS"),sQuery(id+"F0.wireOp",EDGE,"E48.1.0.0"),sQuery(id+"F0.wireOp",EDGE,"E48.1.0.1"),sQuery(id+"F0.wireOp",EDGE,"E48.1.0.2"),sQuery(id+"F0.wireOp",EDGE,"E48.1.0.3"),sQuery(id+"F0.wireOp",EDGE,"E48.1.0.4"),sQuery(id+"F0.wireOp",EDGE,"E48.1.0.5"),sQuery(id+"F0.wireOp",EDGE,"E48.2.0.0"),sQuery(id+"F0.wireOp",EDGE,"E48.2.0.1"),sQuery(id+"F0.wireOp",EDGE,"E48.2.0.2"),sQuery(id+"F0.wireOp",EDGE,"E48.2.0.3"),sQuery(id+"F0.wireOp",EDGE,"E48.2.0.4"),sQuery(id+"F0.wireOp",EDGE,"E48.2.0.5"),sQuery(id+"F0.wireOp",EDGE,"E50.MirrorCS"),sQuery(id+"F0.wireOp",EDGE,"E51.MirrorCS"),sQuery(id+"F0.wireOp",EDGE,"E52.MirrorCS"),sQuery(id+"F0.wireOp",EDGE,"E53.MirrorCS"),sQuery(id+"F0.wireOp",EDGE,"E54.MirrorCS"),sQuery(id+"F0.wireOp",EDGE,"E55.MirrorCS"),sQuery(id+"F0.wireOp",EDGE,"E56.MirrorCS"),sQuery(id+"F0.wireOp",EDGE,"E57.MirrorCS"),sQuery(id+"F0.wireOp",EDGE,"E58.MirrorCS"),sQuery(id+"F0.wireOp",EDGE,"E60.MirrorCS"),sQuery(id+"F0.wireOp",EDGE,"E61.MirrorCS"),sQuery(id+"F0.wireOp",EDGE,"E62.MirrorCS")])],"isStart":false});
            var sketch = newSketch(context, id + "F8", { "sketchPlane" : qUnion([Q0])});
            skLineSegment(sketch, "E102.bottom", {"start": v(-87.63, 95.11) * mm, "end": v(-83.63, 95.11) * mm});
            skLineSegment(sketch, "E102.top", {"start": v(-87.63, -37.89) * mm, "end": v(-83.63, -37.89) * mm});
            skLineSegment(sketch, "E102.left", {"start": v(-87.63, 95.11) * mm, "end": v(-87.63, -37.89) * mm});
            skLineSegment(sketch, "E102.right", {"start": v(-83.63, 95.11) * mm, "end": v(-83.63, -37.89) * mm});
            skPoint(sketch, "E103.oppositeSnap0", {"position": v(88.37, 71.11) * mm});
            skLineSegment(sketch, "E103.bottom", {"start": v(92.37, -37.89) * mm, "end": v(88.37, -37.89) * mm});
            skLineSegment(sketch, "E103.top", {"start": v(92.37, 95.11) * mm, "end": v(88.37, 95.11) * mm});
            skLineSegment(sketch, "E103.left", {"start": v(92.37, -37.89) * mm, "end": v(92.37, 95.11) * mm});
            skLineSegment(sketch, "E103.right", {"start": v(88.37, -37.89) * mm, "end": v(88.37, 95.11) * mm});
            skLineSegment(sketch, "E104.bottom", {"start": v(-57.63, -39.89) * mm, "end": v(62.37, -39.89) * mm});
            skLineSegment(sketch, "E104.top", {"start": v(-57.63, -35.89) * mm, "end": v(62.37, -35.89) * mm});
            skLineSegment(sketch, "E104.left", {"start": v(-57.63, -39.89) * mm, "end": v(-57.63, -35.89) * mm});
            skLineSegment(sketch, "E104.right", {"start": v(62.37, -39.89) * mm, "end": v(62.37, -35.89) * mm});
            skLineSegment(sketch, "E105.bottom", {"start": v(-57.63, -35.89) * mm, "end": v(-57.63, -35.89) * mm});
            skLineSegment(sketch, "E105.top", {"start": v(-57.63, -39.89) * mm, "end": v(-57.63, -39.89) * mm});
            skLineSegment(sketch, "E105.left", {"start": v(-57.63, -35.89) * mm, "end": v(-57.63, -39.89) * mm});
            skLineSegment(sketch, "E105.right", {"start": v(-57.63, -35.89) * mm, "end": v(-57.63, -39.89) * mm});
            skLineSegment(sketch, "E106.bottom", {"start": v(-57.63, -35.89) * mm, "end": v(-61.63, -35.89) * mm});
            skLineSegment(sketch, "E106.top", {"start": v(-57.63, -94.89) * mm, "end": v(-61.63, -94.89) * mm});
            skLineSegment(sketch, "E106.left", {"start": v(-57.63, -35.89) * mm, "end": v(-57.63, -94.89) * mm});
            skLineSegment(sketch, "E106.right", {"start": v(-61.63, -35.89) * mm, "end": v(-61.63, -94.89) * mm});
            skLineSegment(sketch, "E107.bottom", {"start": v(62.37, -35.89) * mm, "end": v(66.37, -35.89) * mm});
            skLineSegment(sketch, "E107.top", {"start": v(62.37, -94.89) * mm, "end": v(66.37, -94.89) * mm});
            skLineSegment(sketch, "E107.left", {"start": v(62.37, -35.89) * mm, "end": v(62.37, -94.89) * mm});
            skLineSegment(sketch, "E107.right", {"start": v(66.37, -35.89) * mm, "end": v(66.37, -94.89) * mm});
            skSolve(sketch);
        }
        {
            var Q0;
            Q0=qSketchRegion(id+"F8",true);
            extrude(context, id + "F9", {"entities" : qUnion([Q0]), "depth" : 50 * mm});
        }
    });
